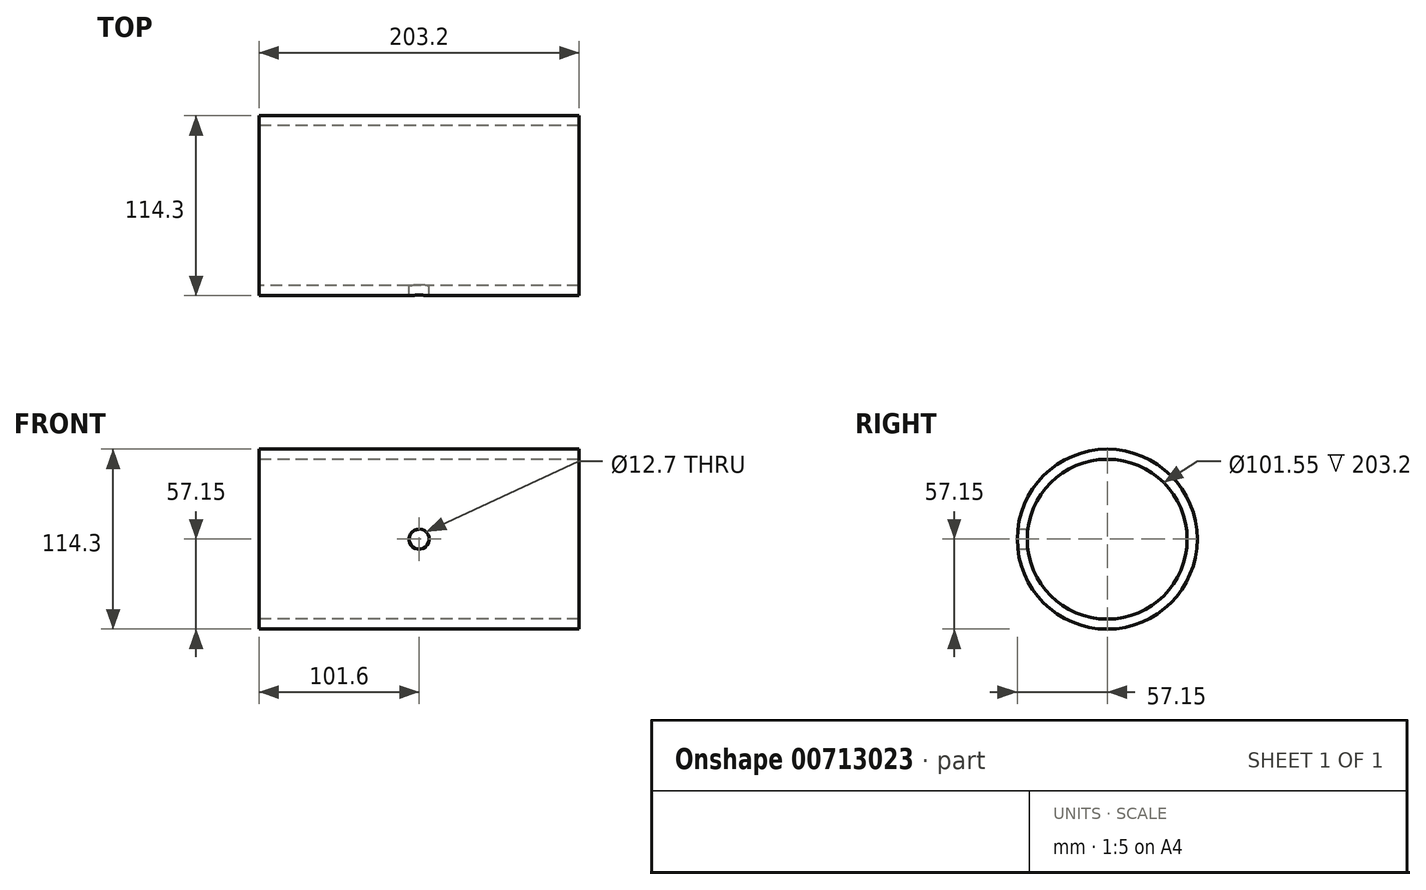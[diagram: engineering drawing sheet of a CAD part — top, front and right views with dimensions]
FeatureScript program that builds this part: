
annotation { "Feature Type Name" : "Feature", "Feature Type Description" : "" }
export const myFeature = defineFeature(function(context is Context, id is Id, definition is map)
    precondition{}
    {
        {
            var Q0;
            Q0=qCreatedBy(makeId("Right.planeOp"),FACE);
            var sketch = newSketch(context, id + "F0", { "sketchPlane" : qUnion([Q0])});
            skCircle(sketch, "E0", {"center": v(0, 0) * mm, "radius": 57.15 * mm});
            skCircle(sketch, "E1", {"center": v(0, 0) * mm, "radius": 50.77 * mm});
            skSolve(sketch);
        }
        {
            var Q0;
            Q0 = qSketchRegion(id + "F0", true);
            extrude(context, id + "F1", {"entities" : qUnion([Q0]), "endBound" : BoundingType.SYMMETRIC, "depth" : 203.2 * mm, "offsetDistance" : 25.4 * mm});
        }
        {
            var Q0;
            Q0=qCreatedBy(makeId("Front.planeOp"),FACE);
            var sketch = newSketch(context, id + "F2", { "sketchPlane" : qUnion([Q0])});
            skCircle(sketch, "E2", {"center": v(0, 0) * mm, "radius": 6.35 * mm});
            skSolve(sketch);
        }
        {
            var Q0;
            Q0 = qSketchRegion(id + "F2", true);
            extrude(context, id + "F3", {"entities" : qUnion([Q0]), "operationType" : NewBodyOperationType.REMOVE, "endBound" : BoundingType.THROUGH_ALL, "depth" : 25.4 * mm, "offsetDistance" : 25.4 * mm});
        }
    });
